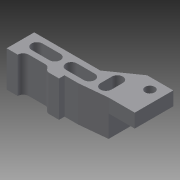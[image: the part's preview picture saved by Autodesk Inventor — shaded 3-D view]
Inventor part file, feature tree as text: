
AUTODESK INVENTOR PART (.ipt)
format: ipt  version: 2015 (Build 190159000, 159)  size: 157,184 bytes
history: native  units: in
note: dims shown in document units (in); Inventor stores cm internally (conversion verified against a paired STEP export)
features: extrude x2, sketch x1, fillet x1
ambient origin geometry x8: Origin, YZ Plane, XZ Plane, XY Plane, X Axis, Y Axis, Z Axis, Center Point
bodies: Body1 (feature_tree)
feature tree (4):
  sketch  "Sketch1"  dims[d6=0.315in d7=0.1969in d8=0.0787in d9=0.1969in d10=0.0787in d11=0.3937in d12=0.0787in d13=0.1575in d15=0.1969in d16=0.1575in d17=0.1575in d18=0.1181in d19=0.1181in d20=0.1575in d21=0.1575in d36=0.3937in d37=0.1772in d38=0.1378in d39=0.1575in d40=0.1575in d41=0.1181in d42=0.1575in d43=0.1575in d44=0.1575in d45=0.315in d46=0.0in d47=0.1969in d48=0.0in d49=0.0787in]
  extrude  "Extrusion3"  Depth=0.1969in
  extrude  "Extrusion4"  Depth=0.0787in
  fillet  "Fillet2"  Radius=0.1969in
